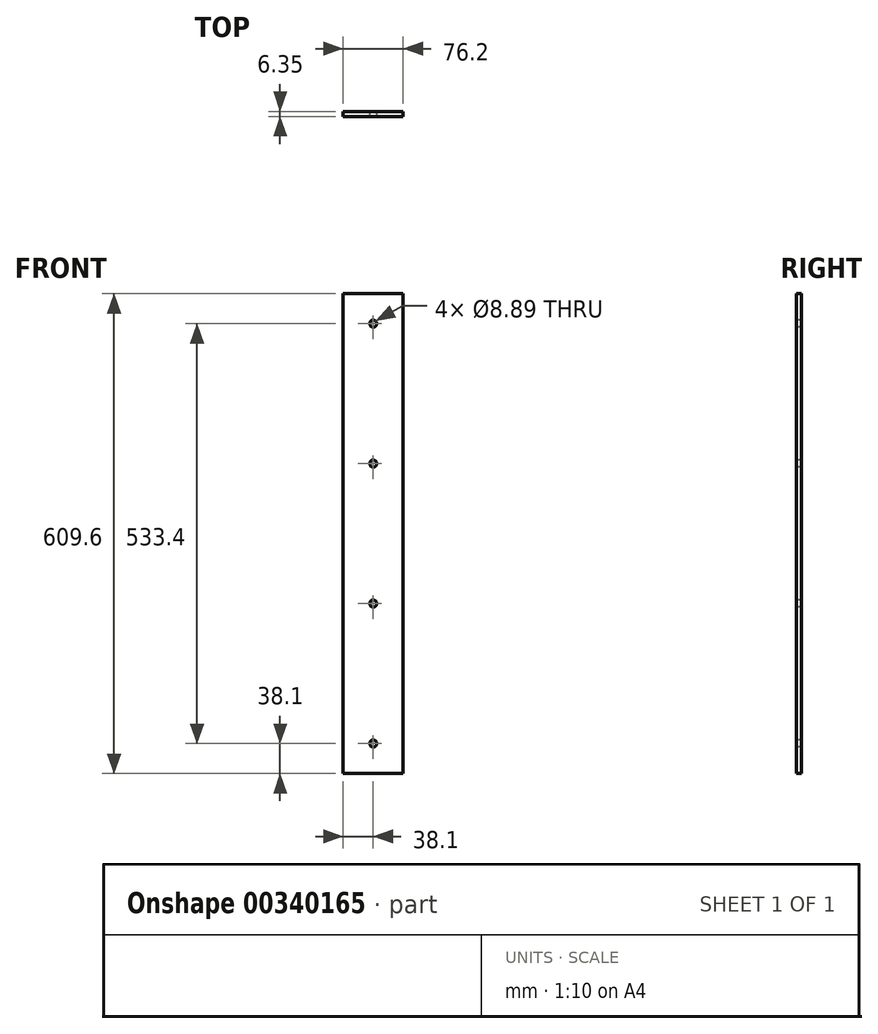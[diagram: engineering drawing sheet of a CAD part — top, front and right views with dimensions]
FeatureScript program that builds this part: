
annotation { "Feature Type Name" : "Feature", "Feature Type Description" : "" }
export const myFeature = defineFeature(function(context is Context, id is Id, definition is map)
    precondition{}
    {
        {
            var Q0;
            Q0=qCreatedBy(makeId("Front.planeOp"),FACE);
            var sketch = newSketch(context, id + "F0", { "sketchPlane" : qUnion([Q0])});
            skLineSegment(sketch, "E0.bottom", {"start": v(0, 0) * mm, "end": v(76.2, 0) * mm});
            skLineSegment(sketch, "E0.top", {"start": v(0, 609.6) * mm, "end": v(76.2, 609.6) * mm});
            skLineSegment(sketch, "E0.left", {"start": v(0, 0) * mm, "end": v(0, 609.6) * mm});
            skLineSegment(sketch, "E0.right", {"start": v(76.2, 0) * mm, "end": v(76.2, 609.6) * mm});
            skSolve(sketch);
        }
        {
            var Q0;
            Q0 = qSketchRegion(id + "F0", true);
            extrude(context, id + "F1", {"entities" : qUnion([Q0]), "depth" : 6.35 * mm});
        }
        {
            var Q0;
            Q0=makeQuery(id+"F1.opExtrude","CAP_FACE",FACE,{"disambiguationData":[OSD([sQuery(id+"F0.wireOp",EDGE,"E0.bottom"),sQuery(id+"F0.wireOp",EDGE,"E0.top"),sQuery(id+"F0.wireOp",EDGE,"E0.left"),sQuery(id+"F0.wireOp",EDGE,"E0.right")])],"isStart":false});
            var sketch = newSketch(context, id + "F2", { "sketchPlane" : qUnion([Q0])});
            skLineSegment(sketch, "E1", {"start": v(38.1, 0) * mm, "end": v(38.1, 38.1) * mm, "construction": true});
            skLineSegment(sketch, "E2", {"start": v(38.1, 38.1) * mm, "end": v(38.1, 215.9) * mm, "construction": true});
            skLineSegment(sketch, "E3", {"start": v(38.1, 215.9) * mm, "end": v(38.1, 393.7) * mm, "construction": true});
            skLineSegment(sketch, "E4", {"start": v(38.1, 393.7) * mm, "end": v(38.1, 571.5) * mm, "construction": true});
            skLineSegment(sketch, "E5", {"start": v(38.1, 571.5) * mm, "end": v(38.1, 609.6) * mm, "construction": true});
            skCircle(sketch, "E6", {"center": v(38.1, 571.5) * mm, "radius": 4.45 * mm});
            skCircle(sketch, "E7", {"center": v(38.1, 393.7) * mm, "radius": 4.45 * mm});
            skCircle(sketch, "E8", {"center": v(38.1, 215.9) * mm, "radius": 4.45 * mm});
            skCircle(sketch, "E9", {"center": v(38.1, 38.1) * mm, "radius": 4.44 * mm});
            skSolve(sketch);
        }
        {
            var Q0;
            Q0 = qSketchRegion(id + "F2", true);
            extrude(context, id + "F3", {"entities" : qUnion([Q0]), "operationType" : NewBodyOperationType.REMOVE, "endBound" : BoundingType.THROUGH_ALL, "oppositeDirection" : true, "depth" : 25.4 * mm});
        }
    });
